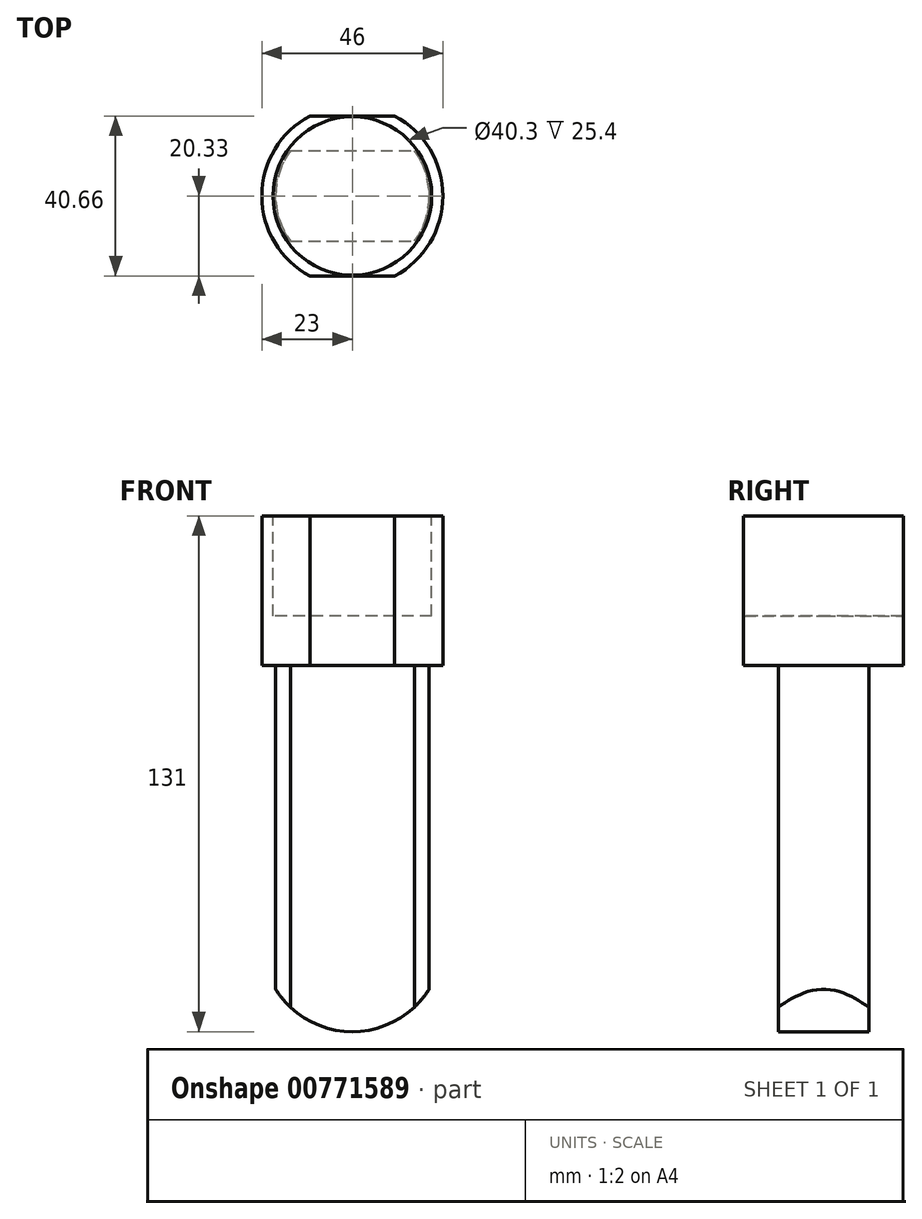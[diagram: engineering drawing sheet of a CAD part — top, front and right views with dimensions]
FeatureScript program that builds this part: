
annotation { "Feature Type Name" : "Feature", "Feature Type Description" : "" }
export const myFeature = defineFeature(function(context is Context, id is Id, definition is map)
    precondition{}
    {
        {
            var Q0;
            Q0=qCreatedBy(makeId("Top.planeOp"),FACE);
            var sketch = newSketch(context, id + "F0", { "sketchPlane" : qUnion([Q0])});
            skArc(sketch, "E0", {"start": v(-10.75, 20.33) * mm, "mid": v(-23, 0) * mm, "end": v(-10.75, -20.33) * mm});
            skLineSegment(sketch, "E1", {"start": v(-10.75, 20.33) * mm, "end": v(10.75, 20.33) * mm});
            skLineSegment(sketch, "E2.MirrorCS", {"start": v(-10.75, -20.33) * mm, "end": v(10.75, -20.33) * mm});
            skArc(sketch, "E3.trimOffspring", {"start": v(10.75, -20.33) * mm, "mid": v(23, 0) * mm, "end": v(10.75, 20.33) * mm});
            skSolve(sketch);
        }
        {
            var Q0;
            Q0=makeQuery(id+"F0.imprint","IMPRINT",FACE,{"disambiguationData":[TD([[makeQuery(id+"F0.imprint","IMPRINT",EDGE,{"derivedFrom":sQuery(id+"F0.wireOp",EDGE,"E0")}),1.0]])]});
            extrude(context, id + "F1", {"entities" : qUnion([Q0]), "depth" : 38 * mm, "offsetDistance" : 25.4 * mm});
        }
        {
            var Q0;
            Q0=makeQuery(id+"F1.opExtrude","CAP_FACE",FACE,{"disambiguationData":[OSD([sQuery(id+"F0.wireOp",EDGE,"E0"),sQuery(id+"F0.wireOp",EDGE,"E1"),sQuery(id+"F0.wireOp",EDGE,"E2.MirrorCS"),sQuery(id+"F0.wireOp",EDGE,"E3.trimOffspring")])],"isStart":false});
            var sketch = newSketch(context, id + "F2", { "sketchPlane" : qUnion([Q0])});
            skCircle(sketch, "E4", {"center": v(0, 0) * mm, "radius": 20.15 * mm});
            skSolve(sketch);
        }
        {
            var Q0;
            Q0=qSketchRegion(id+"F2",true);
            extrude(context, id + "F3", {"entities" : qUnion([Q0]), "operationType" : NewBodyOperationType.REMOVE, "oppositeDirection" : true, "depth" : 25.4 * mm, "offsetDistance" : 25.4 * mm});
        }
        {
            var Q0;
            Q0=makeQuery(id+"F1.opExtrude","CAP_FACE",FACE,{"disambiguationData":[OSD([sQuery(id+"F0.wireOp",EDGE,"E0"),sQuery(id+"F0.wireOp",EDGE,"E1"),sQuery(id+"F0.wireOp",EDGE,"E2.MirrorCS"),sQuery(id+"F0.wireOp",EDGE,"E3.trimOffspring")])],"isStart":true});
            var sketch = newSketch(context, id + "F4", { "sketchPlane" : qUnion([Q0])});
            skArc(sketch, "E5", {"start": v(-15.75, 11.5) * mm, "mid": v(-19.5, 0) * mm, "end": v(-15.75, -11.5) * mm});
            skLineSegment(sketch, "E6", {"start": v(-15.75, 11.5) * mm, "end": v(15.75, 11.5) * mm});
            skLineSegment(sketch, "E7.MirrorCS", {"start": v(-15.75, -11.5) * mm, "end": v(15.75, -11.5) * mm});
            skArc(sketch, "E8.trimOffspring", {"start": v(15.75, -11.5) * mm, "mid": v(19.5, 0) * mm, "end": v(15.75, 11.5) * mm});
            skSolve(sketch);
        }
        {
            var Q0;
            Q0=makeQuery(id+"F4.imprint","IMPRINT",FACE,{"disambiguationData":[TD([[makeQuery(id+"F4.imprint","IMPRINT",EDGE,{"derivedFrom":sQuery(id+"F4.wireOp",EDGE,"E5")}),1.0]])]});
            extrude(context, id + "F5", {"entities" : qUnion([Q0]), "operationType" : NewBodyOperationType.ADD, "depth" : 93 * mm, "offsetDistance" : 25.4 * mm});
        }
        {
            var Q0;
            Q0=makeQuery(id+"F5.opExtrude","SWEPT_FACE",FACE,{"disambiguationData":[OSD([sQuery(id+"F4.wireOp",EDGE,"E6")])]});
            var sketch = newSketch(context, id + "F6", { "sketchPlane" : qUnion([Q0])});
            skArc(sketch, "E9", {"start": v(-22.12, -76.3) * mm, "mid": v(1.02, -92.98) * mm, "end": v(22.6, -74.3) * mm});
            skLineSegment(sketch, "E10", {"start": v(-22.12, -76.3) * mm, "end": v(-44.18, -110.5) * mm});
            skLineSegment(sketch, "E11", {"start": v(-44.18, -110.5) * mm, "end": v(51.09, -107.82) * mm});
            skLineSegment(sketch, "E12", {"start": v(51.09, -107.82) * mm, "end": v(22.6, -74.3) * mm});
            skSolve(sketch);
        }
        {
            var Q0;
            {var subQ0=sQuery(id+"F6.wireOp",EDGE,"E10");Q0=makeQuery(id+"F6.imprint","IMPRINT",FACE,{"disambiguationData":[TD([[makeQuery(id+"F6.imprint","IMPRINT",EDGE,{"derivedFrom":subQ0}),1.0]])]});}
            var Q1;
            {var subQ0=sQuery(id+"F6.wireOp",EDGE,"E9");var subQ1=sQuery(id+"F4.wireOp",EDGE,"E6");var subQ4=makeQuery(id+"F5.opExtrude","CAP_EDGE",EDGE,{"disambiguationData":[OSD([subQ1])],"isStart":false});var subQ5=makeQuery(id+"F6.imprint","INTERSECT",VERTEX,{"derivedFrom":[subQ4,subQ0]});Q1=makeQuery(id+"F6.imprint","IMPRINT",FACE,{"disambiguationData":[TD([[makeQuery(id+"F6.imprint","IMPRINT",EDGE,{"disambiguationData":[TD([[subQ5,1.0]])],"derivedFrom":subQ0}),-1.0]])]});}
            var Q2;
            {var subQ0=sQuery(id+"F6.wireOp",EDGE,"E9");var subQ1=sQuery(id+"F4.wireOp",EDGE,"E6");var subQ4=makeQuery(id+"F5.opExtrude","CAP_EDGE",EDGE,{"disambiguationData":[OSD([subQ1])],"isStart":false});var subQ5=makeQuery(id+"F6.imprint","INTERSECT",VERTEX,{"derivedFrom":[subQ4,subQ0]});Q2=makeQuery(id+"F6.imprint","IMPRINT",FACE,{"disambiguationData":[TD([[makeQuery(id+"F6.imprint","IMPRINT",EDGE,{"disambiguationData":[TD([[subQ5,-1.0]])],"derivedFrom":subQ0}),-1.0]])]});}
            extrude(context, id + "F7", {"entities" : qUnion([Q0, Q1, Q2]), "operationType" : NewBodyOperationType.REMOVE, "endBound" : BoundingType.THROUGH_ALL, "oppositeDirection" : true, "depth" : 25.4 * mm, "offsetDistance" : 25.4 * mm});
        }
    });
